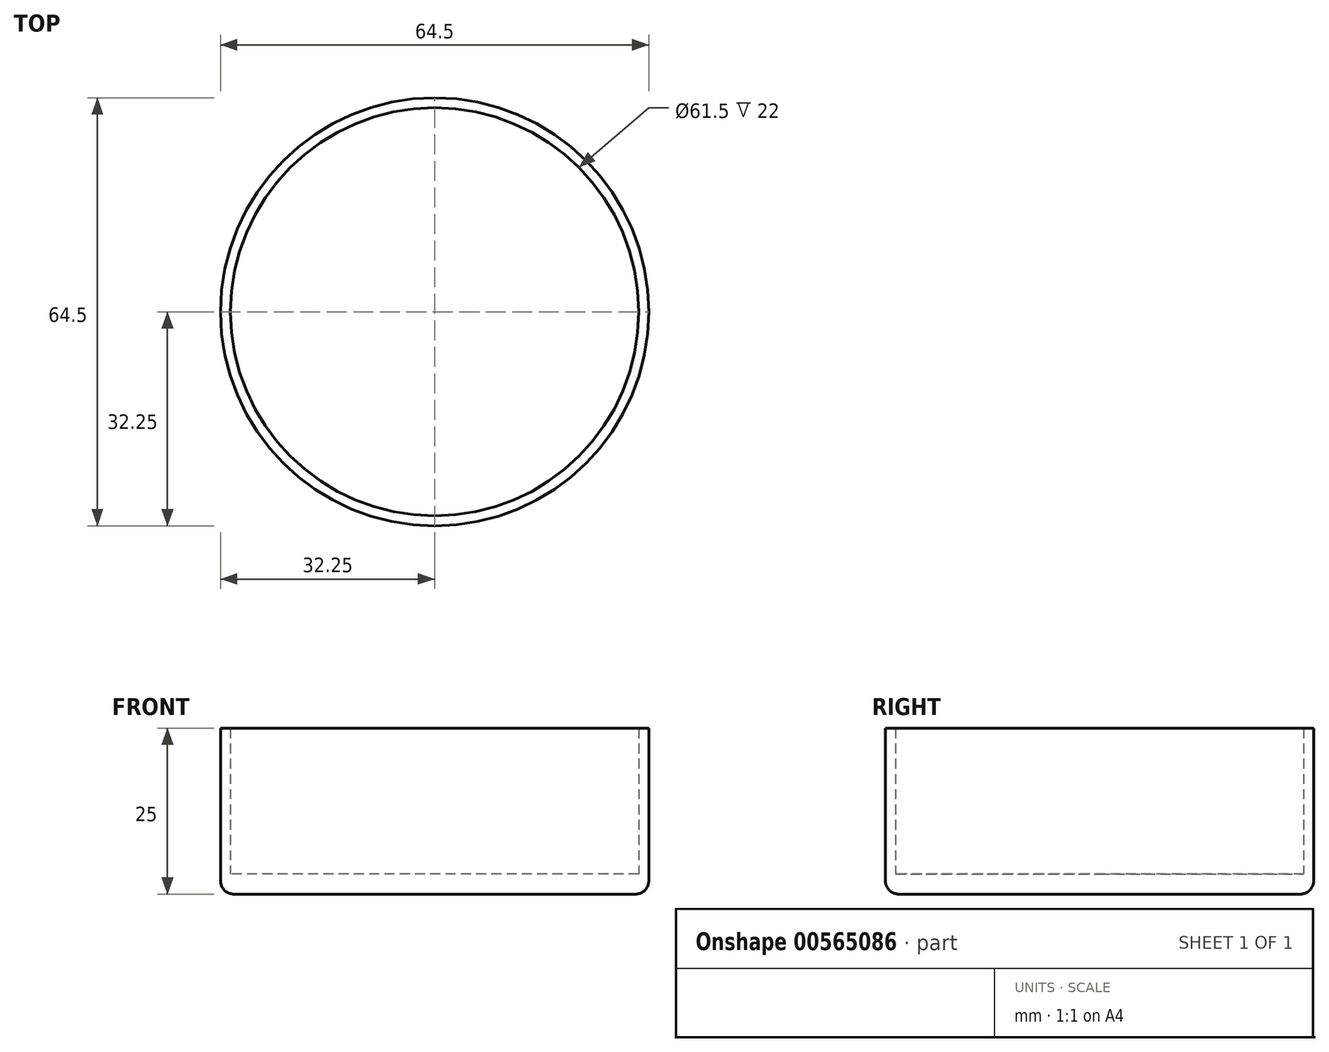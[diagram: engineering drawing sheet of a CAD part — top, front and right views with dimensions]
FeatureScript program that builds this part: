
annotation { "Feature Type Name" : "Feature", "Feature Type Description" : "" }
export const myFeature = defineFeature(function(context is Context, id is Id, definition is map)
    precondition{}
    {
        {
            var Q0;
            Q0=qCreatedBy(makeId("Top.planeOp"),FACE);
            var sketch = newSketch(context, id + "F0", { "sketchPlane" : qUnion([Q0])});
            skCircle(sketch, "E0", {"center": v(0, 0) * mm, "radius": 32.25 * mm});
            skCircle(sketch, "E1", {"center": v(0, 0) * mm, "radius": 30.75 * mm});
            skSolve(sketch);
        }
        {
            var Q0;
            Q0 = qSketchRegion(id + "F0", true);
            extrude(context, id + "F1", {"entities" : qUnion([Q0]), "depth" : 22 * mm, "offsetDistance" : 25 * mm});
        }
        {
            var Q0;
            Q0=qCreatedBy(makeId("Top.planeOp"),FACE);
            var sketch = newSketch(context, id + "F2", { "sketchPlane" : qUnion([Q0])});
            skCircle(sketch, "E2.0", {"center": v(0, 0) * mm, "radius": 32.25 * mm});
            skSolve(sketch);
        }
        {
            var Q0;
            Q0 = qSketchRegion(id + "F2", true);
            extrude(context, id + "F3", {"entities" : qUnion([Q0]), "operationType" : NewBodyOperationType.ADD, "oppositeDirection" : true, "depth" : 3 * mm, "offsetDistance" : 25 * mm});
        }
        {
            var Q0;
            Q0=makeQuery(id+"F3.opExtrude","CAP_EDGE",EDGE,{"disambiguationData":[OSD([sQuery(id+"F2.wireOp",EDGE,"E2.0")])],"isStart":false});
            fillet(context, id + "F4", {"entities" : qUnion([Q0]), "radius" : 2 * mm, "tangentPropagation" : true, "allowEdgeOverflow" : false});
        }
    });
